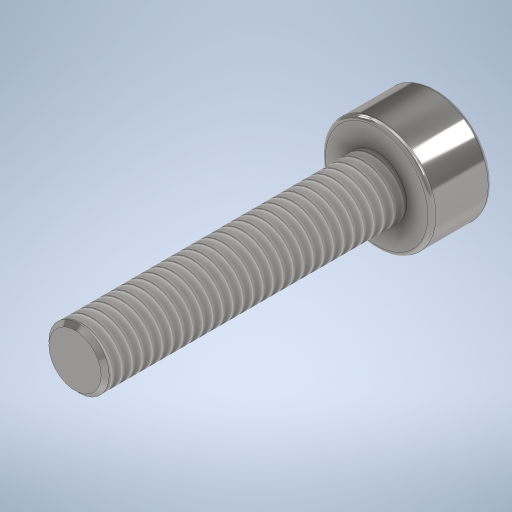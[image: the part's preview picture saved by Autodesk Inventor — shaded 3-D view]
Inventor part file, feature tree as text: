
AUTODESK INVENTOR PART (.ipt)
format: ipt  version: 2023 (Build 270158000, 158)  size: 320,512 bytes
history: native  units: mm
features: extrude x3, sketch x3, other x2, chamfer x1, fillet x1
ambient origin geometry x8: Origin, YZ Plane, XZ Plane, XY Plane, X Axis, Y Axis, Z Axis, Center Point
bodies: Body1 (feature_tree)
feature tree (10):
  other  "솔리드1"
  extrude  "돌출1"  Depth=3.0mm
  chamfer  "모따기1"  Distance=15.0mm
  extrude  "돌출2"  Depth=0.2mm TaperAngle=45.0deg
  fillet  "모깎기1"  Radius=5.5mm
  extrude  "돌출3"  Depth=3.0mm TaperAngle=0.0deg
  other  "스레드1"
  sketch  "스케치1"
  sketch  "스케치2"
  sketch  "스케치3"
